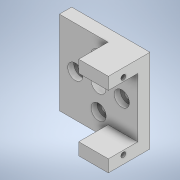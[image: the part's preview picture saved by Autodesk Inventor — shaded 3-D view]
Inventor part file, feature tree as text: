
AUTODESK INVENTOR PART (.ipt)
format: ipt  version: 2020 (Build 240168000, 168)  size: 356,864 bytes
history: native  units: in
note: dims shown in document units (in); Inventor stores cm internally (conversion verified against a paired STEP export)
features: extrude x7, sketch x7
ambient origin geometry x8: Origin, YZ Plane, XZ Plane, XY Plane, X Axis, Y Axis, Z Axis, Center Point
bodies: Solid1 (feature_tree)
feature tree (14):
  extrude  "Extrusion1"  Depth=1.2598in
  extrude  "Extrusion2"  Depth=0.1181in
  extrude  "Extrusion3"  Depth=1.5748in TaperAngle=360.0deg
  extrude  "Extrusion4"  Depth=0.1969in
  extrude  "Extrusion5"  Depth=0.0984in TaperAngle=0.0deg
  extrude  "Extrusion6"  Depth=0.1969in
  extrude  "Extrusion7"  Depth=0.4724in TaperAngle=0.0deg
  sketch  "Sketch1"  dims[d1=1.2598in d2=1.2598in]
  sketch  "Sketch2"  dims[d3=0.1969in d4=0.0in d5=0.1181in]
  sketch  "Sketch3"  dims[d6=0.374in d7=1.5748in d9=360.0deg]
  sketch  "Sketch4"  dims[d11=0.1969in d12=0.0in d13=0.2441in]
  sketch  "Sketch5"  dims[d14=1.5748in d16=360.0deg d18=0.0984in d19=0.0in]
  sketch  "Sketch8"  dims[d20=0.4764in d21=0.1969in]
  sketch  "Sketch9"  dims[d22=0.1969in d23=0.4724in d24=0.0in d25=0.2362in d26=0.3937in d27=0.0in d28=0.4764in d29=0.4764in d30=1.2598in d31=0.0433in d32=1.2598in d33=0.0433in d34=0.1969in d35=0.0in d36=0.2323in d37=0.5394in d38=0.0787in d39=0.5906in d40=0.0in]
